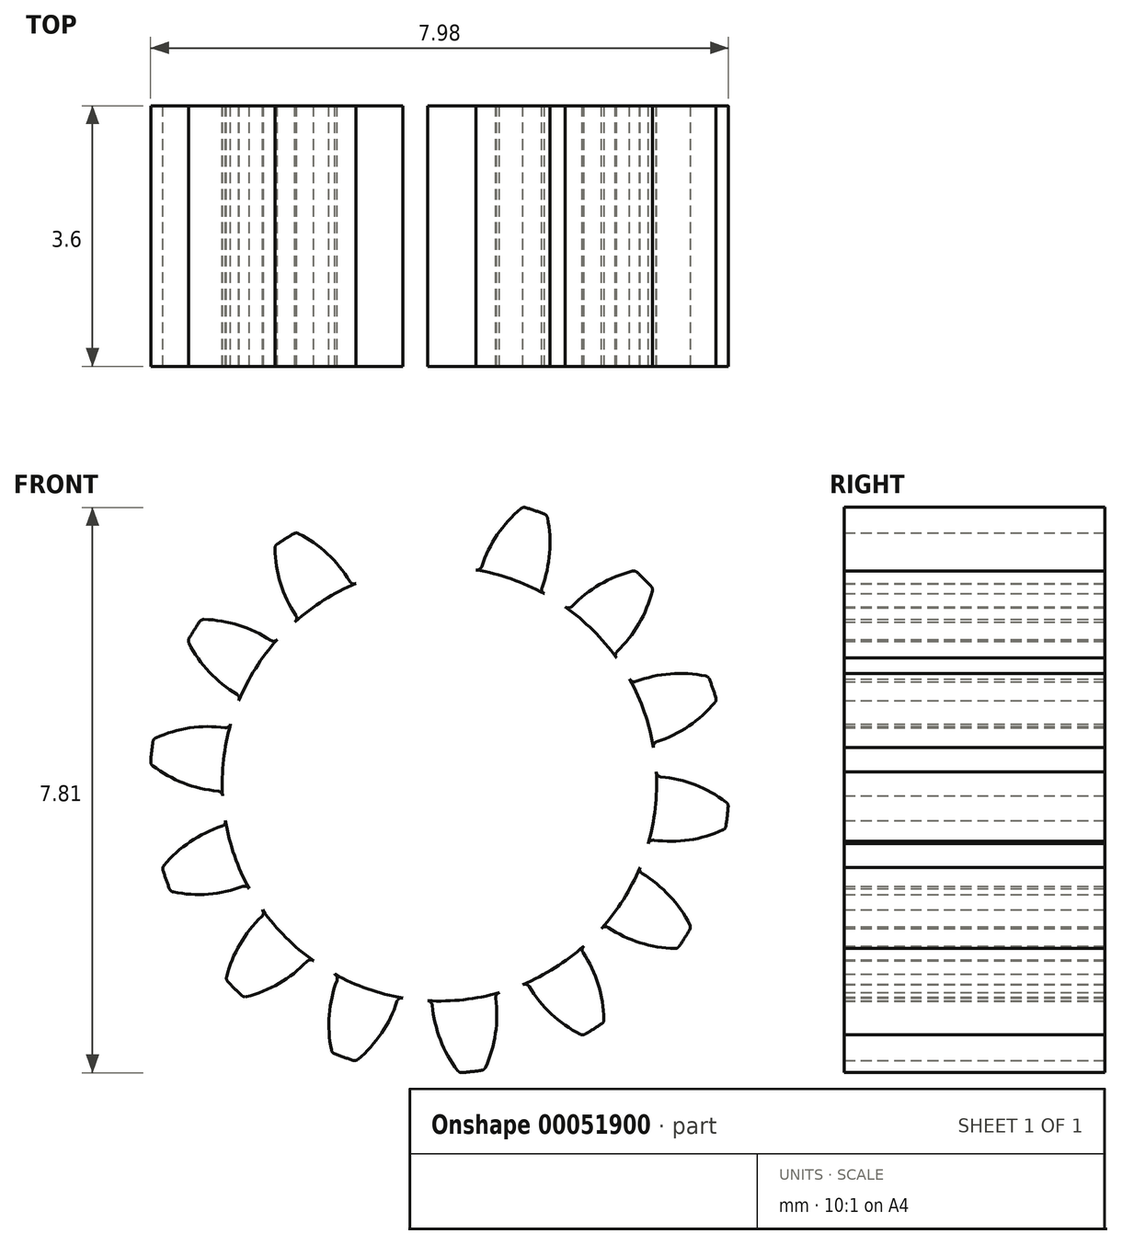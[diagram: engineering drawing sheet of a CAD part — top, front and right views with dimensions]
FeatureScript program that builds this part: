
annotation { "Feature Type Name" : "Feature", "Feature Type Description" : "" }
export const myFeature = defineFeature(function(context is Context, id is Id, definition is map)
    precondition{}
    {
        {
            var Q0;
            Q0=qCreatedBy(makeId("Front.planeOp"),FACE);
            var sketch = newSketch(context, id + "F0", { "sketchPlane" : qUnion([Q0])});
            skCircle(sketch, "E0", {"center": v(0, 0) * mm, "radius": 3 * mm, "construction": true});
            skCircle(sketch, "E1", {"center": v(0, 0) * mm, "radius": 3.5 * mm, "construction": true});
            skCircle(sketch, "E2", {"center": v(0, 0) * mm, "radius": 4 * mm, "construction": true});
            skLineSegment(sketch, "E3", {"start": v(0, 8.23) * mm, "end": v(0, 0) * mm, "construction": true});
            skCircle(sketch, "E4.cCircle", {"center": v(0, 0) * mm, "radius": 8.23 * mm, "construction": true});
            skLineSegment(sketch, "E4.0", {"start": v(0, 8.23) * mm, "end": v(1.83, 8.03) * mm, "construction": true});
            skLineSegment(sketch, "E4.1", {"start": v(1.83, 8.03) * mm, "end": v(3.57, 7.42) * mm, "construction": true});
            skLineSegment(sketch, "E4.2", {"start": v(3.57, 7.42) * mm, "end": v(5.13, 6.44) * mm, "construction": true});
            skLineSegment(sketch, "E4.3", {"start": v(5.13, 6.44) * mm, "end": v(6.44, 5.13) * mm, "construction": true});
            skLineSegment(sketch, "E4.4", {"start": v(6.44, 5.13) * mm, "end": v(7.42, 3.57) * mm, "construction": true});
            skLineSegment(sketch, "E4.5", {"start": v(7.42, 3.57) * mm, "end": v(8.03, 1.83) * mm, "construction": true});
            skLineSegment(sketch, "E4.6", {"start": v(8.03, 1.83) * mm, "end": v(8.23, 0) * mm, "construction": true});
            skLineSegment(sketch, "E4.7", {"start": v(8.23, 0) * mm, "end": v(8.03, -1.83) * mm, "construction": true});
            skLineSegment(sketch, "E4.8", {"start": v(8.03, -1.83) * mm, "end": v(7.42, -3.57) * mm, "construction": true});
            skLineSegment(sketch, "E4.9", {"start": v(7.42, -3.57) * mm, "end": v(6.44, -5.13) * mm, "construction": true});
            skLineSegment(sketch, "E4.10", {"start": v(6.44, -5.13) * mm, "end": v(5.13, -6.44) * mm, "construction": true});
            skLineSegment(sketch, "E4.11", {"start": v(5.13, -6.44) * mm, "end": v(3.57, -7.42) * mm, "construction": true});
            skLineSegment(sketch, "E4.12", {"start": v(3.57, -7.42) * mm, "end": v(1.83, -8.03) * mm, "construction": true});
            skLineSegment(sketch, "E4.13", {"start": v(1.83, -8.03) * mm, "end": v(0, -8.23) * mm, "construction": true});
            skLineSegment(sketch, "E4.14", {"start": v(0, -8.23) * mm, "end": v(-1.83, -8.03) * mm, "construction": true});
            skLineSegment(sketch, "E4.15", {"start": v(-1.83, -8.03) * mm, "end": v(-3.57, -7.42) * mm, "construction": true});
            skLineSegment(sketch, "E4.16", {"start": v(-3.57, -7.42) * mm, "end": v(-5.13, -6.44) * mm, "construction": true});
            skLineSegment(sketch, "E4.17", {"start": v(-5.13, -6.44) * mm, "end": v(-6.44, -5.13) * mm, "construction": true});
            skLineSegment(sketch, "E4.18", {"start": v(-6.44, -5.13) * mm, "end": v(-7.42, -3.57) * mm, "construction": true});
            skLineSegment(sketch, "E4.19", {"start": v(-7.42, -3.57) * mm, "end": v(-8.03, -1.83) * mm, "construction": true});
            skLineSegment(sketch, "E4.20", {"start": v(-8.03, -1.83) * mm, "end": v(-8.23, 0) * mm, "construction": true});
            skLineSegment(sketch, "E4.21", {"start": v(-8.23, 0) * mm, "end": v(-8.03, 1.83) * mm, "construction": true});
            skLineSegment(sketch, "E4.22", {"start": v(-8.03, 1.83) * mm, "end": v(-7.42, 3.57) * mm, "construction": true});
            skLineSegment(sketch, "E4.23", {"start": v(-7.42, 3.57) * mm, "end": v(-6.44, 5.13) * mm, "construction": true});
            skLineSegment(sketch, "E4.24", {"start": v(-6.44, 5.13) * mm, "end": v(-5.13, 6.44) * mm, "construction": true});
            skLineSegment(sketch, "E4.25", {"start": v(-5.13, 6.44) * mm, "end": v(-3.57, 7.42) * mm, "construction": true});
            skLineSegment(sketch, "E4.26", {"start": v(-3.57, 7.42) * mm, "end": v(-1.83, 8.03) * mm, "construction": true});
            skLineSegment(sketch, "E4.27", {"start": v(-1.83, 8.03) * mm, "end": v(0, 8.23) * mm, "construction": true});
            skLineSegment(sketch, "E5.0", {"start": v(-0.93, 8.23) * mm, "end": v(0.93, 8.23) * mm, "construction": true});
            skLineSegment(sketch, "E5.1", {"start": v(0.93, 8.23) * mm, "end": v(2.74, 7.82) * mm, "construction": true});
            skLineSegment(sketch, "E5.2", {"start": v(2.74, 7.82) * mm, "end": v(4.4, 7.02) * mm, "construction": true});
            skLineSegment(sketch, "E5.3", {"start": v(4.4, 7.02) * mm, "end": v(5.86, 5.86) * mm});
            skLineSegment(sketch, "E5.4", {"start": v(5.86, 5.86) * mm, "end": v(7.02, 4.4) * mm});
            skLineSegment(sketch, "E5.5", {"start": v(7.02, 4.4) * mm, "end": v(7.82, 2.74) * mm});
            skLineSegment(sketch, "E5.6", {"start": v(7.82, 2.74) * mm, "end": v(8.23, 0.93) * mm});
            skLineSegment(sketch, "E5.7", {"start": v(8.23, 0.93) * mm, "end": v(8.23, -0.93) * mm});
            skLineSegment(sketch, "E5.8", {"start": v(8.23, -0.93) * mm, "end": v(7.82, -2.74) * mm});
            skLineSegment(sketch, "E5.9", {"start": v(7.82, -2.74) * mm, "end": v(7.02, -4.4) * mm});
            skLineSegment(sketch, "E5.10", {"start": v(7.02, -4.4) * mm, "end": v(5.86, -5.86) * mm});
            skLineSegment(sketch, "E5.11", {"start": v(5.86, -5.86) * mm, "end": v(4.4, -7.02) * mm});
            skLineSegment(sketch, "E5.12", {"start": v(4.4, -7.02) * mm, "end": v(2.74, -7.82) * mm});
            skLineSegment(sketch, "E5.13", {"start": v(2.74, -7.82) * mm, "end": v(0.93, -8.23) * mm});
            skLineSegment(sketch, "E5.14", {"start": v(0.93, -8.23) * mm, "end": v(-0.93, -8.23) * mm});
            skLineSegment(sketch, "E5.15", {"start": v(-0.93, -8.23) * mm, "end": v(-2.74, -7.82) * mm});
            skLineSegment(sketch, "E5.16", {"start": v(-2.74, -7.82) * mm, "end": v(-4.4, -7.02) * mm});
            skLineSegment(sketch, "E5.17", {"start": v(-4.4, -7.02) * mm, "end": v(-5.86, -5.86) * mm});
            skLineSegment(sketch, "E5.18", {"start": v(-5.86, -5.86) * mm, "end": v(-7.02, -4.4) * mm});
            skLineSegment(sketch, "E5.19", {"start": v(-7.02, -4.4) * mm, "end": v(-7.82, -2.74) * mm});
            skLineSegment(sketch, "E5.20", {"start": v(-7.82, -2.74) * mm, "end": v(-8.23, -0.93) * mm});
            skLineSegment(sketch, "E5.21", {"start": v(-8.23, -0.93) * mm, "end": v(-8.23, 0.93) * mm});
            skLineSegment(sketch, "E5.22", {"start": v(-8.23, 0.93) * mm, "end": v(-7.82, 2.74) * mm});
            skLineSegment(sketch, "E5.23", {"start": v(-7.82, 2.74) * mm, "end": v(-7.02, 4.4) * mm});
            skLineSegment(sketch, "E5.24", {"start": v(-7.02, 4.4) * mm, "end": v(-5.86, 5.86) * mm});
            skLineSegment(sketch, "E5.25", {"start": v(-5.86, 5.86) * mm, "end": v(-4.4, 7.02) * mm, "construction": true});
            skLineSegment(sketch, "E5.26", {"start": v(-4.4, 7.02) * mm, "end": v(-2.74, 7.82) * mm, "construction": true});
            skLineSegment(sketch, "E5.27", {"start": v(-2.74, 7.82) * mm, "end": v(-0.93, 8.23) * mm, "construction": true});
            skPoint(sketch, "E5.0.midPoint", {"position": v(0, 8.23) * mm});
            skLineSegment(sketch, "E6", {"start": v(-0.93, 8.23) * mm, "end": v(0, 0) * mm, "construction": true});
            skLineSegment(sketch, "E7", {"start": v(0, 3.5) * mm, "end": v(-9.32, 3.5) * mm, "construction": true});
            skLineSegment(sketch, "E8", {"start": v(0, 3.5) * mm, "end": v(-9.62, 0) * mm, "construction": true});
            skCircle(sketch, "E9", {"center": v(0, 3.5) * mm, "radius": 1.75 * mm, "construction": true});
            skCircle(sketch, "E10", {"center": v(-1.64, 2.9) * mm, "radius": 1.75 * mm, "construction": true});
            skArc(sketch, "E11", {"start": v(-0.25, 3.96) * mm, "mid": v(-0.01, 3.53) * mm, "end": v(0.1, 3.06) * mm});
            skArc(sketch, "E12.MirrorCS", {"start": v(-0.62, 3.95) * mm, "mid": v(-0.78, 3.44) * mm, "end": v(-0.77, 2.9) * mm});
            skArc(sketch, "E13.MirrorCS", {"start": v(-0.64, 3.92) * mm, "mid": v(-0.77, 3.45) * mm, "end": v(-0.78, 2.96) * mm});
            skArc(sketch, "E14", {"start": v(-0.58, 3.96) * mm, "mid": v(-0.45, 3.97) * mm, "end": v(-0.31, 3.99) * mm});
            skArc(sketch, "E15", {"start": v(-0.83, 2.88) * mm, "mid": v(0.34, -2.98) * mm, "end": v(0.16, 3) * mm});
            skPoint(sketch, "E16.visualSharp", {"position": v(-0.77, 2.9) * mm});
            skArc(sketch, "E16.filletArc", {"start": v(-0.83, 2.88) * mm, "mid": v(-0.79, 2.91) * mm, "end": v(-0.78, 2.96) * mm});
            skPoint(sketch, "E17.visualSharp", {"position": v(0.1, 3) * mm});
            skArc(sketch, "E17.filletArc", {"start": v(0.1, 3.06) * mm, "mid": v(0.12, 3.02) * mm, "end": v(0.16, 3) * mm});
            skPoint(sketch, "E18.visualSharp", {"position": v(-0.62, 3.95) * mm});
            skArc(sketch, "E18.filletArc", {"start": v(-0.58, 3.96) * mm, "mid": v(-0.61, 3.94) * mm, "end": v(-0.64, 3.92) * mm});
            skPoint(sketch, "E19.visualSharp", {"position": v(-0.27, 4) * mm});
            skArc(sketch, "E19.filletArc", {"start": v(-0.25, 3.96) * mm, "mid": v(-0.28, 3.98) * mm, "end": v(-0.31, 3.99) * mm});
            skArc(sketch, "E20.1.0", {"start": v(-2.27, 3.25) * mm, "mid": v(-2.2, 2.77) * mm, "end": v(-1.98, 2.33) * mm});
            skArc(sketch, "E20.1.1", {"start": v(-2, 2.24) * mm, "mid": v(-1.97, 2.28) * mm, "end": v(-1.98, 2.33) * mm});
            skArc(sketch, "E20.1.2", {"start": v(-2.24, 3.31) * mm, "mid": v(-2.27, 3.29) * mm, "end": v(-2.27, 3.25) * mm});
            skArc(sketch, "E20.1.3", {"start": v(-2.24, 3.31) * mm, "mid": v(-2.13, 3.39) * mm, "end": v(-2.01, 3.46) * mm});
            skArc(sketch, "E20.1.4", {"start": v(-1.94, 3.46) * mm, "mid": v(-1.55, 3.18) * mm, "end": v(-1.24, 2.8) * mm});
            skArc(sketch, "E20.1.5", {"start": v(-1.94, 3.46) * mm, "mid": v(-1.98, 3.47) * mm, "end": v(-2.01, 3.46) * mm});
            skArc(sketch, "E20.1.6", {"start": v(-1.24, 2.8) * mm, "mid": v(-1.2, 2.77) * mm, "end": v(-1.15, 2.77) * mm});
            skArc(sketch, "E20.2.0", {"start": v(-3.46, 1.94) * mm, "mid": v(-3.18, 1.55) * mm, "end": v(-2.8, 1.24) * mm});
            skArc(sketch, "E20.2.1", {"start": v(-2.77, 1.15) * mm, "mid": v(-2.77, 1.2) * mm, "end": v(-2.8, 1.24) * mm});
            skArc(sketch, "E20.2.2", {"start": v(-3.46, 2.01) * mm, "mid": v(-3.47, 1.98) * mm, "end": v(-3.46, 1.94) * mm});
            skArc(sketch, "E20.2.3", {"start": v(-3.46, 2.01) * mm, "mid": v(-3.39, 2.13) * mm, "end": v(-3.31, 2.24) * mm});
            skArc(sketch, "E20.2.4", {"start": v(-3.25, 2.27) * mm, "mid": v(-2.77, 2.2) * mm, "end": v(-2.33, 1.98) * mm});
            skArc(sketch, "E20.2.5", {"start": v(-3.25, 2.27) * mm, "mid": v(-3.29, 2.27) * mm, "end": v(-3.31, 2.24) * mm});
            skArc(sketch, "E20.2.6", {"start": v(-2.33, 1.98) * mm, "mid": v(-2.28, 1.97) * mm, "end": v(-2.24, 2) * mm});
            skArc(sketch, "E20.3.0", {"start": v(-3.96, 0.25) * mm, "mid": v(-3.53, 0.01) * mm, "end": v(-3.06, -0.1) * mm});
            skArc(sketch, "E20.3.1", {"start": v(-3, -0.16) * mm, "mid": v(-3.02, -0.12) * mm, "end": v(-3.06, -0.1) * mm});
            skArc(sketch, "E20.3.2", {"start": v(-3.99, 0.31) * mm, "mid": v(-3.98, 0.28) * mm, "end": v(-3.96, 0.25) * mm});
            skArc(sketch, "E20.3.3", {"start": v(-3.99, 0.31) * mm, "mid": v(-3.97, 0.45) * mm, "end": v(-3.96, 0.58) * mm});
            skArc(sketch, "E20.3.4", {"start": v(-3.92, 0.64) * mm, "mid": v(-3.45, 0.77) * mm, "end": v(-2.96, 0.78) * mm});
            skArc(sketch, "E20.3.5", {"start": v(-3.92, 0.64) * mm, "mid": v(-3.94, 0.61) * mm, "end": v(-3.96, 0.58) * mm});
            skArc(sketch, "E20.3.6", {"start": v(-2.96, 0.78) * mm, "mid": v(-2.91, 0.79) * mm, "end": v(-2.88, 0.83) * mm});
            skArc(sketch, "E20.4.0", {"start": v(-3.68, -1.5) * mm, "mid": v(-3.19, -1.52) * mm, "end": v(-2.71, -1.42) * mm});
            skArc(sketch, "E20.4.1", {"start": v(-2.63, -1.45) * mm, "mid": v(-2.66, -1.42) * mm, "end": v(-2.71, -1.42) * mm});
            skArc(sketch, "E20.4.2", {"start": v(-3.73, -1.45) * mm, "mid": v(-3.7, -1.48) * mm, "end": v(-3.68, -1.5) * mm});
            skArc(sketch, "E20.4.3", {"start": v(-3.73, -1.45) * mm, "mid": v(-3.78, -1.32) * mm, "end": v(-3.82, -1.2) * mm});
            skArc(sketch, "E20.4.4", {"start": v(-3.8, -1.13) * mm, "mid": v(-3.44, -0.8) * mm, "end": v(-3, -0.58) * mm});
            skArc(sketch, "E20.4.5", {"start": v(-3.8, -1.13) * mm, "mid": v(-3.82, -1.16) * mm, "end": v(-3.82, -1.2) * mm});
            skArc(sketch, "E20.4.6", {"start": v(-3, -0.58) * mm, "mid": v(-2.97, -0.55) * mm, "end": v(-2.96, -0.5) * mm});
            skArc(sketch, "E20.5.0", {"start": v(-2.67, -2.94) * mm, "mid": v(-2.21, -2.76) * mm, "end": v(-1.83, -2.45) * mm});
            skArc(sketch, "E20.5.1", {"start": v(-1.74, -2.44) * mm, "mid": v(-1.79, -2.43) * mm, "end": v(-1.83, -2.45) * mm});
            skArc(sketch, "E20.5.2", {"start": v(-2.73, -2.92) * mm, "mid": v(-2.7, -2.94) * mm, "end": v(-2.67, -2.94) * mm});
            skArc(sketch, "E20.5.3", {"start": v(-2.73, -2.92) * mm, "mid": v(-2.83, -2.83) * mm, "end": v(-2.92, -2.73) * mm});
            skArc(sketch, "E20.5.4", {"start": v(-2.94, -2.67) * mm, "mid": v(-2.76, -2.21) * mm, "end": v(-2.45, -1.83) * mm});
            skArc(sketch, "E20.5.5", {"start": v(-2.94, -2.67) * mm, "mid": v(-2.94, -2.7) * mm, "end": v(-2.92, -2.73) * mm});
            skArc(sketch, "E20.5.6", {"start": v(-2.45, -1.83) * mm, "mid": v(-2.43, -1.79) * mm, "end": v(-2.44, -1.74) * mm});
            skArc(sketch, "E20.6.0", {"start": v(-1.13, -3.8) * mm, "mid": v(-0.8, -3.44) * mm, "end": v(-0.58, -3) * mm});
            skArc(sketch, "E20.6.1", {"start": v(-0.5, -2.96) * mm, "mid": v(-0.55, -2.97) * mm, "end": v(-0.58, -3) * mm});
            skArc(sketch, "E20.6.2", {"start": v(-1.2, -3.82) * mm, "mid": v(-1.16, -3.82) * mm, "end": v(-1.13, -3.8) * mm});
            skArc(sketch, "E20.6.3", {"start": v(-1.2, -3.82) * mm, "mid": v(-1.32, -3.78) * mm, "end": v(-1.45, -3.73) * mm});
            skArc(sketch, "E20.6.4", {"start": v(-1.5, -3.68) * mm, "mid": v(-1.52, -3.19) * mm, "end": v(-1.42, -2.71) * mm});
            skArc(sketch, "E20.6.5", {"start": v(-1.5, -3.68) * mm, "mid": v(-1.48, -3.7) * mm, "end": v(-1.45, -3.73) * mm});
            skArc(sketch, "E20.6.6", {"start": v(-1.42, -2.71) * mm, "mid": v(-1.42, -2.66) * mm, "end": v(-1.45, -2.63) * mm});
            skArc(sketch, "E20.7.0", {"start": v(0.64, -3.92) * mm, "mid": v(0.77, -3.45) * mm, "end": v(0.78, -2.96) * mm});
            skArc(sketch, "E20.7.1", {"start": v(0.83, -2.88) * mm, "mid": v(0.79, -2.91) * mm, "end": v(0.78, -2.96) * mm});
            skArc(sketch, "E20.7.2", {"start": v(0.58, -3.96) * mm, "mid": v(0.61, -3.94) * mm, "end": v(0.64, -3.92) * mm});
            skArc(sketch, "E20.7.3", {"start": v(0.58, -3.96) * mm, "mid": v(0.45, -3.97) * mm, "end": v(0.31, -3.99) * mm});
            skArc(sketch, "E20.7.4", {"start": v(0.25, -3.96) * mm, "mid": v(0.01, -3.53) * mm, "end": v(-0.1, -3.06) * mm});
            skArc(sketch, "E20.7.5", {"start": v(0.25, -3.96) * mm, "mid": v(0.28, -3.98) * mm, "end": v(0.31, -3.99) * mm});
            skArc(sketch, "E20.7.6", {"start": v(-0.1, -3.06) * mm, "mid": v(-0.12, -3.02) * mm, "end": v(-0.16, -3) * mm});
            skArc(sketch, "E20.8.0", {"start": v(2.27, -3.25) * mm, "mid": v(2.2, -2.77) * mm, "end": v(1.98, -2.33) * mm});
            skArc(sketch, "E20.8.1", {"start": v(2, -2.24) * mm, "mid": v(1.97, -2.28) * mm, "end": v(1.98, -2.33) * mm});
            skArc(sketch, "E20.8.2", {"start": v(2.24, -3.31) * mm, "mid": v(2.27, -3.29) * mm, "end": v(2.27, -3.25) * mm});
            skArc(sketch, "E20.8.3", {"start": v(2.24, -3.31) * mm, "mid": v(2.13, -3.39) * mm, "end": v(2.01, -3.46) * mm});
            skArc(sketch, "E20.8.4", {"start": v(1.94, -3.46) * mm, "mid": v(1.55, -3.18) * mm, "end": v(1.24, -2.8) * mm});
            skArc(sketch, "E20.8.5", {"start": v(1.94, -3.46) * mm, "mid": v(1.98, -3.47) * mm, "end": v(2.01, -3.46) * mm});
            skArc(sketch, "E20.8.6", {"start": v(1.24, -2.8) * mm, "mid": v(1.2, -2.77) * mm, "end": v(1.15, -2.77) * mm});
            skArc(sketch, "E20.9.0", {"start": v(3.46, -1.94) * mm, "mid": v(3.18, -1.55) * mm, "end": v(2.8, -1.24) * mm});
            skArc(sketch, "E20.9.1", {"start": v(2.77, -1.15) * mm, "mid": v(2.77, -1.2) * mm, "end": v(2.8, -1.24) * mm});
            skArc(sketch, "E20.9.2", {"start": v(3.46, -2.01) * mm, "mid": v(3.47, -1.98) * mm, "end": v(3.46, -1.94) * mm});
            skArc(sketch, "E20.9.3", {"start": v(3.46, -2.01) * mm, "mid": v(3.39, -2.13) * mm, "end": v(3.31, -2.24) * mm});
            skArc(sketch, "E20.9.4", {"start": v(3.25, -2.27) * mm, "mid": v(2.77, -2.2) * mm, "end": v(2.33, -1.98) * mm});
            skArc(sketch, "E20.9.5", {"start": v(3.25, -2.27) * mm, "mid": v(3.29, -2.27) * mm, "end": v(3.31, -2.24) * mm});
            skArc(sketch, "E20.9.6", {"start": v(2.33, -1.98) * mm, "mid": v(2.28, -1.97) * mm, "end": v(2.24, -2) * mm});
            skArc(sketch, "E20.10.0", {"start": v(3.96, -0.25) * mm, "mid": v(3.53, -0.01) * mm, "end": v(3.06, 0.1) * mm});
            skArc(sketch, "E20.10.1", {"start": v(3, 0.16) * mm, "mid": v(3.02, 0.12) * mm, "end": v(3.06, 0.1) * mm});
            skArc(sketch, "E20.10.2", {"start": v(3.99, -0.31) * mm, "mid": v(3.98, -0.28) * mm, "end": v(3.96, -0.25) * mm});
            skArc(sketch, "E20.10.3", {"start": v(3.99, -0.31) * mm, "mid": v(3.97, -0.45) * mm, "end": v(3.96, -0.58) * mm});
            skArc(sketch, "E20.10.4", {"start": v(3.92, -0.64) * mm, "mid": v(3.45, -0.77) * mm, "end": v(2.96, -0.78) * mm});
            skArc(sketch, "E20.10.5", {"start": v(3.92, -0.64) * mm, "mid": v(3.94, -0.61) * mm, "end": v(3.96, -0.58) * mm});
            skArc(sketch, "E20.10.6", {"start": v(2.96, -0.78) * mm, "mid": v(2.91, -0.79) * mm, "end": v(2.88, -0.83) * mm});
            skArc(sketch, "E20.11.0", {"start": v(3.68, 1.5) * mm, "mid": v(3.19, 1.52) * mm, "end": v(2.71, 1.42) * mm});
            skArc(sketch, "E20.11.1", {"start": v(2.63, 1.45) * mm, "mid": v(2.66, 1.42) * mm, "end": v(2.71, 1.42) * mm});
            skArc(sketch, "E20.11.2", {"start": v(3.73, 1.45) * mm, "mid": v(3.7, 1.48) * mm, "end": v(3.68, 1.5) * mm});
            skArc(sketch, "E20.11.3", {"start": v(3.73, 1.45) * mm, "mid": v(3.78, 1.32) * mm, "end": v(3.82, 1.2) * mm});
            skArc(sketch, "E20.11.4", {"start": v(3.8, 1.13) * mm, "mid": v(3.44, 0.8) * mm, "end": v(3, 0.58) * mm});
            skArc(sketch, "E20.11.5", {"start": v(3.8, 1.13) * mm, "mid": v(3.82, 1.16) * mm, "end": v(3.82, 1.2) * mm});
            skArc(sketch, "E20.11.6", {"start": v(3, 0.58) * mm, "mid": v(2.97, 0.55) * mm, "end": v(2.96, 0.5) * mm});
            skArc(sketch, "E20.12.0", {"start": v(2.67, 2.94) * mm, "mid": v(2.21, 2.76) * mm, "end": v(1.83, 2.45) * mm});
            skArc(sketch, "E20.12.1", {"start": v(1.74, 2.44) * mm, "mid": v(1.79, 2.43) * mm, "end": v(1.83, 2.45) * mm});
            skArc(sketch, "E20.12.2", {"start": v(2.73, 2.92) * mm, "mid": v(2.7, 2.94) * mm, "end": v(2.67, 2.94) * mm});
            skArc(sketch, "E20.12.3", {"start": v(2.73, 2.92) * mm, "mid": v(2.83, 2.83) * mm, "end": v(2.92, 2.73) * mm});
            skArc(sketch, "E20.12.4", {"start": v(2.94, 2.67) * mm, "mid": v(2.76, 2.21) * mm, "end": v(2.45, 1.83) * mm});
            skArc(sketch, "E20.12.5", {"start": v(2.94, 2.67) * mm, "mid": v(2.94, 2.7) * mm, "end": v(2.92, 2.73) * mm});
            skArc(sketch, "E20.12.6", {"start": v(2.45, 1.83) * mm, "mid": v(2.43, 1.79) * mm, "end": v(2.44, 1.74) * mm});
            skArc(sketch, "E20.13.0", {"start": v(1.13, 3.8) * mm, "mid": v(0.8, 3.44) * mm, "end": v(0.58, 3) * mm});
            skArc(sketch, "E20.13.1", {"start": v(0.5, 2.96) * mm, "mid": v(0.55, 2.97) * mm, "end": v(0.58, 3) * mm});
            skArc(sketch, "E20.13.2", {"start": v(1.2, 3.82) * mm, "mid": v(1.16, 3.82) * mm, "end": v(1.13, 3.8) * mm});
            skArc(sketch, "E20.13.3", {"start": v(1.2, 3.82) * mm, "mid": v(1.32, 3.78) * mm, "end": v(1.45, 3.73) * mm});
            skArc(sketch, "E20.13.4", {"start": v(1.5, 3.68) * mm, "mid": v(1.52, 3.19) * mm, "end": v(1.42, 2.71) * mm});
            skArc(sketch, "E20.13.5", {"start": v(1.5, 3.68) * mm, "mid": v(1.48, 3.7) * mm, "end": v(1.45, 3.73) * mm});
            skArc(sketch, "E20.13.6", {"start": v(1.42, 2.71) * mm, "mid": v(1.42, 2.66) * mm, "end": v(1.45, 2.63) * mm});
            skSolve(sketch);
        }
        {
            var Q0;
            Q0=makeQuery(id+"F0.imprint","IMPRINT",FACE,{"disambiguationData":[TD([[makeQuery(id+"F0.imprint","IMPRINT",EDGE,{"derivedFrom":sQuery(id+"F0.wireOp",EDGE,"E11")}),-1.0]])]});
            var Q1;
            Q1=makeQuery(id+"F0.imprint","IMPRINT",FACE,{"disambiguationData":[TD([[makeQuery(id+"F0.imprint","IMPRINT",EDGE,{"derivedFrom":sQuery(id+"F0.wireOp",EDGE,"E20.1.0")}),1.0]])]});
            var Q2;
            Q2=makeQuery(id+"F0.imprint","IMPRINT",FACE,{"disambiguationData":[TD([[makeQuery(id+"F0.imprint","IMPRINT",EDGE,{"derivedFrom":sQuery(id+"F0.wireOp",EDGE,"E20.3.0")}),1.0]])]});
            var Q3;
            Q3=makeQuery(id+"F0.imprint","IMPRINT",FACE,{"disambiguationData":[TD([[makeQuery(id+"F0.imprint","IMPRINT",EDGE,{"derivedFrom":sQuery(id+"F0.wireOp",EDGE,"E20.5.0")}),1.0]])]});
            var Q4;
            Q4=makeQuery(id+"F0.imprint","IMPRINT",FACE,{"disambiguationData":[TD([[makeQuery(id+"F0.imprint","IMPRINT",EDGE,{"derivedFrom":sQuery(id+"F0.wireOp",EDGE,"E20.6.0")}),1.0]])]});
            var Q5;
            Q5=makeQuery(id+"F0.imprint","IMPRINT",FACE,{"disambiguationData":[TD([[makeQuery(id+"F0.imprint","IMPRINT",EDGE,{"derivedFrom":sQuery(id+"F0.wireOp",EDGE,"E20.7.0")}),1.0]])]});
            var Q6;
            Q6=makeQuery(id+"F0.imprint","IMPRINT",FACE,{"disambiguationData":[TD([[makeQuery(id+"F0.imprint","IMPRINT",EDGE,{"derivedFrom":sQuery(id+"F0.wireOp",EDGE,"E20.8.0")}),1.0]])]});
            var Q7;
            Q7=makeQuery(id+"F0.imprint","IMPRINT",FACE,{"disambiguationData":[TD([[makeQuery(id+"F0.imprint","IMPRINT",EDGE,{"derivedFrom":sQuery(id+"F0.wireOp",EDGE,"E20.9.0")}),1.0]])]});
            var Q8;
            Q8=makeQuery(id+"F0.imprint","IMPRINT",FACE,{"disambiguationData":[TD([[makeQuery(id+"F0.imprint","IMPRINT",EDGE,{"derivedFrom":sQuery(id+"F0.wireOp",EDGE,"E20.10.0")}),1.0]])]});
            var Q9;
            Q9=makeQuery(id+"F0.imprint","IMPRINT",FACE,{"disambiguationData":[TD([[makeQuery(id+"F0.imprint","IMPRINT",EDGE,{"derivedFrom":sQuery(id+"F0.wireOp",EDGE,"E20.11.0")}),1.0]])]});
            var Q10;
            Q10=makeQuery(id+"F0.imprint","IMPRINT",FACE,{"disambiguationData":[TD([[makeQuery(id+"F0.imprint","IMPRINT",EDGE,{"derivedFrom":sQuery(id+"F0.wireOp",EDGE,"E20.12.0")}),1.0]])]});
            var Q11;
            Q11=makeQuery(id+"F0.imprint","IMPRINT",FACE,{"disambiguationData":[TD([[makeQuery(id+"F0.imprint","IMPRINT",EDGE,{"derivedFrom":sQuery(id+"F0.wireOp",EDGE,"E20.13.0")}),1.0]])]});
            var Q12;
            Q12=makeQuery(id+"F0.imprint","IMPRINT",FACE,{"disambiguationData":[TD([[makeQuery(id+"F0.imprint","IMPRINT",EDGE,{"derivedFrom":sQuery(id+"F0.wireOp",EDGE,"E20.2.0")}),1.0]])]});
            var Q13;
            Q13=makeQuery(id+"F0.imprint","IMPRINT",FACE,{"disambiguationData":[TD([[makeQuery(id+"F0.imprint","IMPRINT",EDGE,{"derivedFrom":sQuery(id+"F0.wireOp",EDGE,"E20.4.0")}),1.0]])]});
            extrude(context, id + "F1", {"entities" : qUnion([Q0, Q1, Q2, Q3, Q4, Q5, Q6, Q7, Q8, Q9, Q10, Q11, Q12, Q13]), "depth" : 3.6 * mm});
        }
        {
            var Q0;
            Q0=makeQuery(id+"F1.opExtrude","CAP_FACE",FACE,{"disambiguationData":[OSD([sQuery(id+"F0.wireOp",EDGE,"E11"),sQuery(id+"F0.wireOp",EDGE,"E13.MirrorCS"),sQuery(id+"F0.wireOp",EDGE,"E14"),sQuery(id+"F0.wireOp",EDGE,"E15"),sQuery(id+"F0.wireOp",EDGE,"E16.filletArc"),sQuery(id+"F0.wireOp",EDGE,"E17.filletArc"),sQuery(id+"F0.wireOp",EDGE,"E18.filletArc"),sQuery(id+"F0.wireOp",EDGE,"E19.filletArc"),sQuery(id+"F0.wireOp",EDGE,"E20.1.0"),sQuery(id+"F0.wireOp",EDGE,"E20.1.1"),sQuery(id+"F0.wireOp",EDGE,"E20.1.2"),sQuery(id+"F0.wireOp",EDGE,"E20.1.3"),sQuery(id+"F0.wireOp",EDGE,"E20.1.4"),sQuery(id+"F0.wireOp",EDGE,"E20.1.5"),sQuery(id+"F0.wireOp",EDGE,"E20.1.6"),sQuery(id+"F0.wireOp",EDGE,"E20.2.0"),sQuery(id+"F0.wireOp",EDGE,"E20.2.1"),sQuery(id+"F0.wireOp",EDGE,"E20.2.2"),sQuery(id+"F0.wireOp",EDGE,"E20.2.3"),sQuery(id+"F0.wireOp",EDGE,"E20.2.4"),sQuery(id+"F0.wireOp",EDGE,"E20.2.5"),sQuery(id+"F0.wireOp",EDGE,"E20.2.6"),sQuery(id+"F0.wireOp",EDGE,"E20.3.0"),sQuery(id+"F0.wireOp",EDGE,"E20.3.1"),sQuery(id+"F0.wireOp",EDGE,"E20.3.2"),sQuery(id+"F0.wireOp",EDGE,"E20.3.3"),sQuery(id+"F0.wireOp",EDGE,"E20.3.4"),sQuery(id+"F0.wireOp",EDGE,"E20.3.5"),sQuery(id+"F0.wireOp",EDGE,"E20.3.6"),sQuery(id+"F0.wireOp",EDGE,"E20.4.0"),sQuery(id+"F0.wireOp",EDGE,"E20.4.1"),sQuery(id+"F0.wireOp",EDGE,"E20.4.2"),sQuery(id+"F0.wireOp",EDGE,"E20.4.3"),sQuery(id+"F0.wireOp",EDGE,"E20.4.4"),sQuery(id+"F0.wireOp",EDGE,"E20.4.5"),sQuery(id+"F0.wireOp",EDGE,"E20.4.6"),sQuery(id+"F0.wireOp",EDGE,"E20.5.0"),sQuery(id+"F0.wireOp",EDGE,"E20.5.1"),sQuery(id+"F0.wireOp",EDGE,"E20.5.2"),sQuery(id+"F0.wireOp",EDGE,"E20.5.3"),sQuery(id+"F0.wireOp",EDGE,"E20.5.4"),sQuery(id+"F0.wireOp",EDGE,"E20.5.5"),sQuery(id+"F0.wireOp",EDGE,"E20.5.6"),sQuery(id+"F0.wireOp",EDGE,"E20.6.0"),sQuery(id+"F0.wireOp",EDGE,"E20.6.1"),sQuery(id+"F0.wireOp",EDGE,"E20.6.2"),sQuery(id+"F0.wireOp",EDGE,"E20.6.3"),sQuery(id+"F0.wireOp",EDGE,"E20.6.4"),sQuery(id+"F0.wireOp",EDGE,"E20.6.5"),sQuery(id+"F0.wireOp",EDGE,"E20.6.6"),sQuery(id+"F0.wireOp",EDGE,"E20.7.0"),sQuery(id+"F0.wireOp",EDGE,"E20.7.1"),sQuery(id+"F0.wireOp",EDGE,"E20.7.2"),sQuery(id+"F0.wireOp",EDGE,"E20.7.3"),sQuery(id+"F0.wireOp",EDGE,"E20.7.4"),sQuery(id+"F0.wireOp",EDGE,"E20.7.5"),sQuery(id+"F0.wireOp",EDGE,"E20.7.6"),sQuery(id+"F0.wireOp",EDGE,"E20.8.0"),sQuery(id+"F0.wireOp",EDGE,"E20.8.1"),sQuery(id+"F0.wireOp",EDGE,"E20.8.2"),sQuery(id+"F0.wireOp",EDGE,"E20.8.3"),sQuery(id+"F0.wireOp",EDGE,"E20.8.4"),sQuery(id+"F0.wireOp",EDGE,"E20.8.5"),sQuery(id+"F0.wireOp",EDGE,"E20.8.6"),sQuery(id+"F0.wireOp",EDGE,"E20.9.0"),sQuery(id+"F0.wireOp",EDGE,"E20.9.1"),sQuery(id+"F0.wireOp",EDGE,"E20.9.2"),sQuery(id+"F0.wireOp",EDGE,"E20.9.3"),sQuery(id+"F0.wireOp",EDGE,"E20.9.4"),sQuery(id+"F0.wireOp",EDGE,"E20.9.5"),sQuery(id+"F0.wireOp",EDGE,"E20.9.6"),sQuery(id+"F0.wireOp",EDGE,"E20.10.0"),sQuery(id+"F0.wireOp",EDGE,"E20.10.1"),sQuery(id+"F0.wireOp",EDGE,"E20.10.2"),sQuery(id+"F0.wireOp",EDGE,"E20.10.3"),sQuery(id+"F0.wireOp",EDGE,"E20.10.4"),sQuery(id+"F0.wireOp",EDGE,"E20.10.5"),sQuery(id+"F0.wireOp",EDGE,"E20.10.6"),sQuery(id+"F0.wireOp",EDGE,"E20.11.0"),sQuery(id+"F0.wireOp",EDGE,"E20.11.1"),sQuery(id+"F0.wireOp",EDGE,"E20.11.2"),sQuery(id+"F0.wireOp",EDGE,"E20.11.3"),sQuery(id+"F0.wireOp",EDGE,"E20.11.4"),sQuery(id+"F0.wireOp",EDGE,"E20.11.5"),sQuery(id+"F0.wireOp",EDGE,"E20.11.6"),sQuery(id+"F0.wireOp",EDGE,"E20.12.0"),sQuery(id+"F0.wireOp",EDGE,"E20.12.1"),sQuery(id+"F0.wireOp",EDGE,"E20.12.2"),sQuery(id+"F0.wireOp",EDGE,"E20.12.3"),sQuery(id+"F0.wireOp",EDGE,"E20.12.4"),sQuery(id+"F0.wireOp",EDGE,"E20.12.5"),sQuery(id+"F0.wireOp",EDGE,"E20.12.6"),sQuery(id+"F0.wireOp",EDGE,"E20.13.0"),sQuery(id+"F0.wireOp",EDGE,"E20.13.1"),sQuery(id+"F0.wireOp",EDGE,"E20.13.2"),sQuery(id+"F0.wireOp",EDGE,"E20.13.3"),sQuery(id+"F0.wireOp",EDGE,"E20.13.4"),sQuery(id+"F0.wireOp",EDGE,"E20.13.5"),sQuery(id+"F0.wireOp",EDGE,"E20.13.6")])],"isStart":false});
            var sketch = newSketch(context, id + "F2", { "sketchPlane" : qUnion([Q0])});
            skCircle(sketch, "E21", {"center": v(0, 0) * mm, "radius": 1 * mm});
            skSolve(sketch);
        }
        {
            var Q0;
            Q0=qSketchRegion(id+"F2",true);
            extrude(context, id + "F3", {"entities" : qUnion([Q0]), "operationType" : NewBodyOperationType.REMOVE, "endBound" : BoundingType.THROUGH_ALL, "oppositeDirection" : true, "depth" : 25 * mm});
        }
    });
